# Revit family: Paulownia tomentosa
name_source: partatom
category: Mass
revit_build: Autodesk Vasari (Build: 20130108_1800)
units: mm (PartAtom-declared; Revit-internal decimal feet)

## types (4) — shared parameters
Default Elevation = 0.00 m

## per-type parameters (varying)
- h albero 20 raggio chioma 8 estate: h albero=20.00 m; h chioma=15.00 m; h tronco=5.00 m; h1=2.00 m; h1r1=3.75 m; h1r3=3.00 m; h2=2.50 m; h2r1=2.50 m; h2r3=4.29 m; h3=4.00 m; h3r3=3.00 m; h4=4.00 m; r1 chioma=0.57 m; r1 ramo1=0.57 m; r1 ramo2=0.57 m; r1 ramo3=0.29 m; r1 ramo4=0.29 m; r1 ramo5=0.57 m; r1 ramo6=0.29 m; r1 tronco=0.71 m; r2 chioma=0.57 m; r2 ramo1=0.29 m; r2 ramo2=0.29 m; r2 ramo3=0.14 m; r2 ramo4=0.19 m; r2 ramo5=0.46 m; r2 ramo6=0.19 m; r2 tronco=0.57 m; r3 ramo1=0.19 m; r3 ramo2=0.19 m; r3 ramo3=0.14 m; r3 ramo4=0.19 m; r4 chioma=8.89 m; r4 ramo2=0.19 m; r5 chioma=8.00 m; r6 chioma=5.33 m; raggio chioma=8.00 m
- h albero 15 raggio chioma 6.24 estate: h albero=15.00 m; h chioma=11.25 m; h tronco=3.75 m; h1=1.50 m; h1r1=2.81 m; h1r3=2.25 m; h2=1.88 m; h2r1=1.88 m; h2r3=3.21 m; h3=3.00 m; h3r3=2.25 m; h4=3.00 m; r1 chioma=0.43 m; r1 ramo1=0.43 m; r1 ramo2=0.43 m; r1 ramo3=0.21 m; r1 ramo4=0.21 m; r1 ramo5=0.43 m; r1 ramo6=0.21 m; r1 tronco=0.54 m; r2 chioma=0.43 m; r2 ramo1=0.21 m; r2 ramo2=0.21 m; r2 ramo3=0.11 m; r2 ramo4=0.14 m; r2 ramo5=0.34 m; r2 ramo6=0.14 m; r2 tronco=0.43 m; r3 ramo1=0.14 m; r3 ramo2=0.14 m; r3 ramo3=0.11 m; r3 ramo4=0.14 m; r4 chioma=6.93 m; r4 ramo2=0.14 m; r5 chioma=6.24 m; r6 chioma=4.16 m; raggio chioma=6.24 m
- h albero 20 raggio chioma 0.5 inverno: h albero=20.00 m; h chioma=15.00 m; h tronco=5.00 m; h1=2.00 m; h1r1=3.75 m; h1r3=3.00 m; h2=2.50 m; h2r1=2.50 m; h2r3=4.29 m; h3=4.00 m; h3r3=3.00 m; h4=4.00 m; r1 chioma=0.57 m; r1 ramo1=0.57 m; r1 ramo2=0.57 m; r1 ramo3=0.29 m; r1 ramo4=0.29 m; r1 ramo5=0.57 m; r1 ramo6=0.29 m; r1 tronco=0.71 m; r2 chioma=0.57 m; r2 ramo1=0.29 m; r2 ramo2=0.29 m; r2 ramo3=0.14 m; r2 ramo4=0.19 m; r2 ramo5=0.46 m; r2 ramo6=0.19 m; r2 tronco=0.57 m; r3 ramo1=0.19 m; r3 ramo2=0.19 m; r3 ramo3=0.14 m; r3 ramo4=0.19 m; r4 chioma=0.56 m; r4 ramo2=0.19 m; r5 chioma=0.50 m; r6 chioma=0.33 m; raggio chioma=0.50 m
- h albero 15 raggio chioma 0.4 inverno: h albero=15.00 m; h chioma=11.25 m; h tronco=3.75 m; h1=1.50 m; h1r1=2.81 m; h1r3=2.25 m; h2=1.88 m; h2r1=1.88 m; h2r3=3.21 m; h3=3.00 m; h3r3=2.25 m; h4=3.00 m; r1 chioma=0.43 m; r1 ramo1=0.43 m; r1 ramo2=0.43 m; r1 ramo3=0.21 m; r1 ramo4=0.21 m; r1 ramo5=0.43 m; r1 ramo6=0.21 m; r1 tronco=0.54 m; r2 chioma=0.43 m; r2 ramo1=0.21 m; r2 ramo2=0.21 m; r2 ramo3=0.11 m; r2 ramo4=0.14 m; r2 ramo5=0.34 m; r2 ramo6=0.14 m; r2 tronco=0.43 m; r3 ramo1=0.14 m; r3 ramo2=0.14 m; r3 ramo3=0.11 m; r3 ramo4=0.14 m; r4 chioma=0.44 m; r4 ramo2=0.14 m; r5 chioma=0.40 m; r6 chioma=0.27 m; raggio chioma=0.40 m

## geometry (parser evidence)
native form markers: Blend x8, Sweep x3
no freeform markers — native parametric forms only
